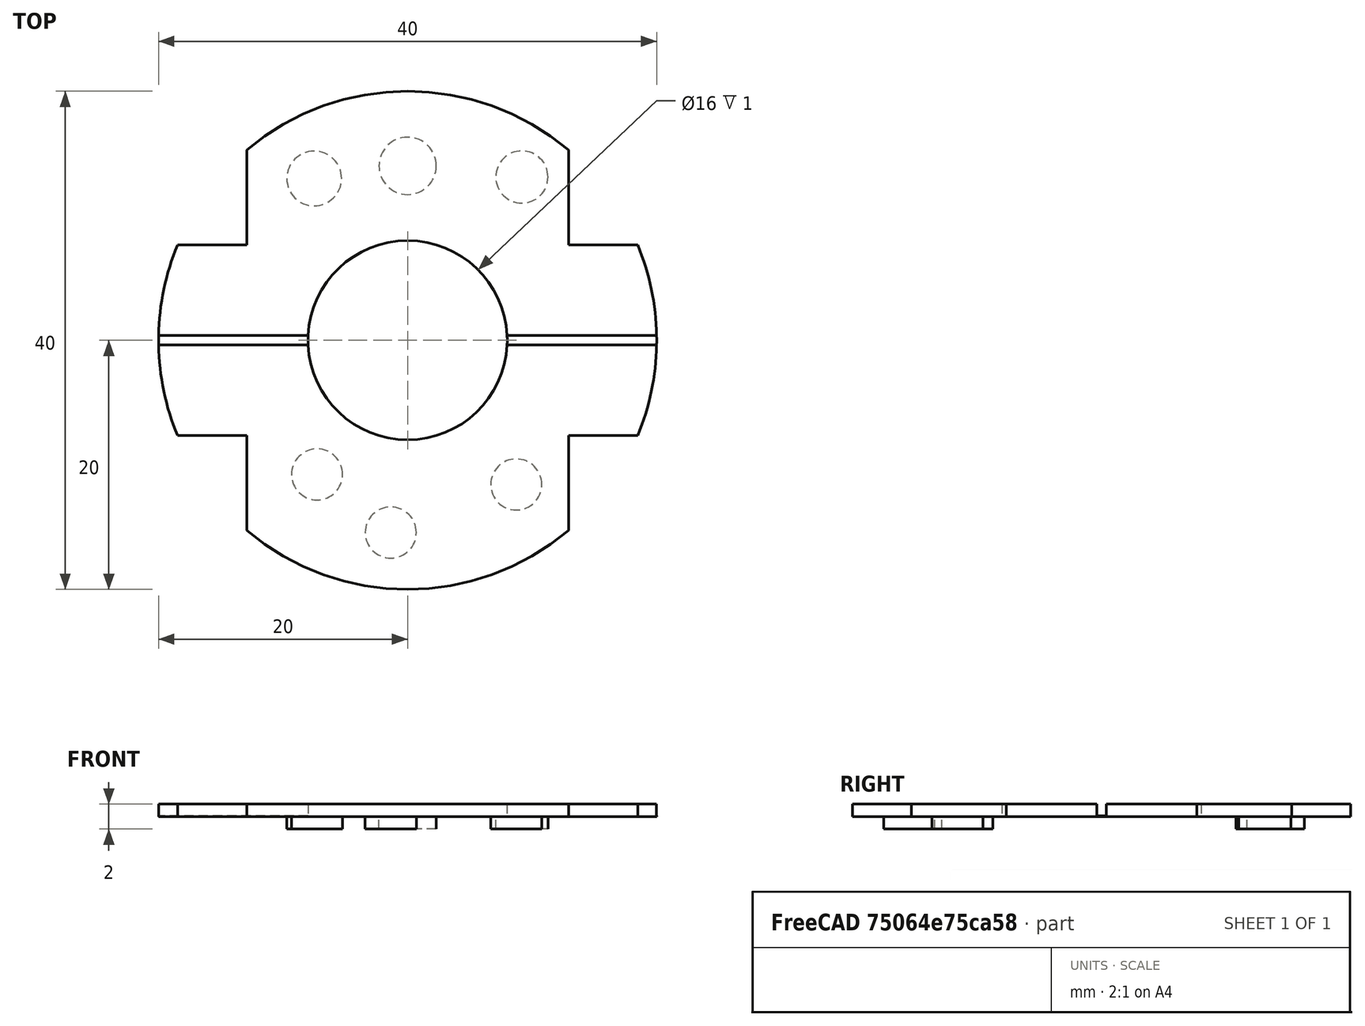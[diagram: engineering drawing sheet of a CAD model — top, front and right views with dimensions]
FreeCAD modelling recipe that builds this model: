
FCSTD DOCUMENT  (FreeCAD 0.19R)
Label: 3.9mmX16.GlueLID
License: All rights reserved
LicenseURL: http://en.wikipedia.org/wiki/All_rights_reserved
objects: Sketcher::SketchObject×4, PartDesign::Pad×2, PartDesign::Pocket×2, PartDesign::Body×1, Mesh::Feature×1
note: 13 computed .brp shape members not serialized (recipe doc carries the construction recipe); baked Part::Feature solids carry a one-line shape summary decoded from their .brp

FEATURE [Sketcher::SketchObject] Sketch
  FullyConstrained = true
  MapMode = 5
  sketch-geometry (2):
    g0: Circle CenterX=0 CenterY=0 CenterZ=0 NormalX=0 NormalY=0 NormalZ=1 AngleXU=0 Radius=20
    g1: Circle CenterX=0 CenterY=0 CenterZ=0 NormalX=0 NormalY=0 NormalZ=1 AngleXU=0 Radius=8
  constraints (4):
    c: Coincident(g0,g-1)
    c: Diameter(g0) = 40
    c: Diameter(g1) = 16
    c: Coincident(g1,g0)
FEATURE [PartDesign::Pad] Pad
  Direction = (1,1,1)
  Length = 1
  Length2 = 100
  Profile = -> Sketch
  Type = 0
FEATURE [Sketcher::SketchObject] Sketch001
  FullyConstrained = true
  MapMode = 5
  Placement = pos=(0,0,1) rot=(0,0,1;0rad)
  Support = -> [Pad]
  sketch-geometry (12):
    g0: Circle CenterX=0 CenterY=14 CenterZ=0 NormalX=0 NormalY=0 NormalZ=1 AngleXU=0 Radius=2.3
    g1: Circle CenterX=0 CenterY=14 CenterZ=0 NormalX=0 NormalY=0 NormalZ=1 AngleXU=0 Radius=1.95
    g2: LineSegment StartX=0 StartY=0 StartZ=0 EndX=14.609 EndY=20.8638 EndZ=0
    g3: LineSegment StartX=0 StartY=0 StartZ=0 EndX=-13.76 EndY=23.833 EndZ=0
    g4: Circle CenterX=-7.5 CenterY=12.9904 CenterZ=0 NormalX=0 NormalY=0 NormalZ=1 AngleXU=0 Radius=2.2
    g5: Circle CenterX=9.17722 CenterY=13.1064 CenterZ=0 NormalX=0 NormalY=0 NormalZ=1 AngleXU=0 Radius=2.1
    g6: LineSegment StartX=0 StartY=0 StartZ=0 EndX=-16.7758 EndY=-24.8711 EndZ=0
    g7: LineSegment StartX=0 StartY=0 StartZ=0 EndX=-1.92789 EndY=-22.0358 EndZ=0
    g8: LineSegment StartX=0 StartY=0 StartZ=0 EndX=15.1718 EndY=-20.1336 EndZ=0
    g9: Circle CenterX=8.72632 CenterY=-11.5802 CenterZ=0 NormalX=0 NormalY=0 NormalZ=1 AngleXU=0 Radius=2.05
    g10: Circle CenterX=-1.35091 CenterY=-15.441 CenterZ=0 NormalX=0 NormalY=0 NormalZ=1 AngleXU=0 Radius=2.05
    g11: Circle CenterX=-7.26951 CenterY=-10.7775 CenterZ=0 NormalX=0 NormalY=0 NormalZ=1 AngleXU=0 Radius=2.05
  constraints (35):
    c: PointOnObject(g0,g-2)
    c: DistanceY(g0) = 14
    c: Diameter(g0) = 4.6
    c: Diameter(g1) = 3.9
    c: Coincident(g1,g0)
    c: Coincident(g2,g-1)
    c: Coincident(g3,g2)
    c: PointOnObject(g5,g2)
    c: PointOnObject(g4,g3)
    c: Distance(g-1,g4) = 15
    c: Distance(g-1,g5) = 16
    c: Angle(g3) = 2.0944
    c: Angle(g2) = 0.959931
    c: Diameter(g4) = 4.4
    c: Diameter(g5) = 4.2
    c: Coincident(g6,g-1)
    c: Coincident(g7,g6)
    c: Coincident(g8,g6)
    c: PointOnObject(g11,g6)
    c: PointOnObject(g10,g7)
    c: PointOnObject(g9,g8)
    c: Distance(g-1,g9) = 14.5
    c: Distance(g-1,g10) = 15.5
    c: Distance(g-1,g11) = 13
    c: Diameter(g11) = 4.1
    c: Equal(g11,g10)
    c: Equal(g11,g9)
    c: Distance(g6) = 30
    c: Angle(g7) = -1.65806
    c: Angle(g6) = -2.16421
    c: Angle(g8) = -0.925025
    c: Distance(g8) = 25.21
    c: Distance(g2) = 25.47
    c: Distance(g3) = 27.52
    c: Distance(g7) = 22.12
FEATURE [PartDesign::Pad] Pad001
  BaseFeature = -> Pad
  Direction = (1,1,1)
  Length = 2
  Length2 = 100
  Profile = -> Sketch001
  Reversed = true
  Type = 0
FEATURE [Sketcher::SketchObject] Sketch004  label="slice"
  FullyConstrained = false
  MapMode = 5
  Placement = pos=(0,0,1) rot=(0,0,1;0rad)
  Support = -> [Pad001]
  sketch-geometry (4):
    g0: LineSegment StartX=-22.2478 StartY=0.375 StartZ=0 EndX=20.7748 EndY=0.375 EndZ=0
    g1: LineSegment StartX=20.7748 StartY=0.375 StartZ=0 EndX=20.7748 EndY=-0.375 EndZ=0
    g2: LineSegment StartX=20.7748 StartY=-0.375 StartZ=0 EndX=-22.2478 EndY=-0.375 EndZ=0
    g3: LineSegment StartX=-22.2478 StartY=-0.375 StartZ=0 EndX=-22.2478 EndY=0.375 EndZ=0
  constraints (9):
    c: Coincident(g0,g1)
    c: Coincident(g1,g2)
    c: Coincident(g2,g3)
    c: Coincident(g3,g0)
    c: Horizontal(g0)
    c: Horizontal(g2)
    c: Vertical(g3)
    c: Distance(g1) = 0.75
    c: Symmetric(g1,g0,g-1)
FEATURE [PartDesign::Pocket] Pocket
  BaseFeature = -> Pad001
  Length = 0.95
  Length2 = 100
  Profile = -> Sketch004
  Type = 0
FEATURE [Sketcher::SketchObject] Sketch007  label="notches"
  FullyConstrained = false
  MapMode = 5
  Placement = pos=(0,0,1) rot=(0,0,1;0rad)
  Support = -> [Pocket]
  sketch-geometry (16):
    g0: LineSegment StartX=-20.5587 StartY=-7.65293 StartZ=0 EndX=-12.9211 EndY=-7.65293 EndZ=0
    g1: LineSegment StartX=-12.9211 StartY=-7.65293 StartZ=0 EndX=-12.9211 EndY=-18.5136 EndZ=0
    g2: LineSegment StartX=-12.9211 StartY=-18.5136 StartZ=0 EndX=-20.5587 EndY=-18.5136 EndZ=0
    g3: LineSegment StartX=-20.5587 StartY=-18.5136 StartZ=0 EndX=-20.5587 EndY=-7.65293 EndZ=0
    g4: LineSegment StartX=-21.1657 StartY=19.7081 StartZ=0 EndX=-12.9211 EndY=19.7081 EndZ=0
    g5: LineSegment StartX=-12.9211 StartY=19.7081 StartZ=0 EndX=-12.9211 EndY=7.65293 EndZ=0
    g6: LineSegment StartX=-12.9211 StartY=7.65293 StartZ=0 EndX=-21.1657 EndY=7.65293 EndZ=0
    g7: LineSegment StartX=-21.1657 StartY=7.65293 StartZ=0 EndX=-21.1657 EndY=19.7081 EndZ=0
    g8: LineSegment StartX=12.9211 StartY=18.5942 StartZ=0 EndX=21.451 EndY=18.5942 EndZ=0
    g9: LineSegment StartX=21.451 StartY=18.5942 StartZ=0 EndX=21.451 EndY=7.65293 EndZ=0
    g10: LineSegment StartX=21.451 StartY=7.65293 StartZ=0 EndX=12.9211 EndY=7.65293 EndZ=0
    g11: LineSegment StartX=12.9211 StartY=7.65293 StartZ=0 EndX=12.9211 EndY=18.5942 EndZ=0
    g12: LineSegment StartX=12.9211 StartY=-7.65293 StartZ=0 EndX=24.754 EndY=-7.65293 EndZ=0
    g13: LineSegment StartX=24.754 StartY=-7.65293 StartZ=0 EndX=24.754 EndY=-18.3213 EndZ=0
    g14: LineSegment StartX=24.754 StartY=-18.3213 StartZ=0 EndX=12.9211 EndY=-18.3213 EndZ=0
    g15: LineSegment StartX=12.9211 StartY=-18.3213 StartZ=0 EndX=12.9211 EndY=-7.65293 EndZ=0
  constraints (35):
    c: Coincident(g0,g1)
    c: Coincident(g1,g2)
    c: Coincident(g2,g3)
    c: Coincident(g3,g0)
    c: Horizontal(g0)
    c: Horizontal(g2)
    c: Vertical(g1)
    c: Vertical(g3)
    c: Coincident(g4,g5)
    c: Coincident(g5,g6)
    c: Coincident(g6,g7)
    c: Coincident(g7,g4)
    c: Horizontal(g4)
    c: Horizontal(g6)
    c: Vertical(g5)
    c: Vertical(g7)
    c: Coincident(g8,g9)
    c: Coincident(g9,g10)
    c: Coincident(g10,g11)
    c: Coincident(g11,g8)
    c: Horizontal(g8)
    c: Horizontal(g10)
    c: Vertical(g9)
    c: Vertical(g11)
    c: Coincident(g12,g13)
    c: Coincident(g13,g14)
    c: Coincident(g14,g15)
    c: Coincident(g15,g12)
    c: Horizontal(g12)
    c: Horizontal(g14)
    c: Vertical(g13)
    c: Vertical(g15)
    c: Symmetric(g12,g0,g-2)
    c: Symmetric(g10,g0,g-1)
    c: Symmetric(g5,g12,g-1)
FEATURE [PartDesign::Pocket] Pocket001
  BaseFeature = -> Pocket
  Length = 5
  Length2 = 100
  Profile = -> Sketch007
  Type = 0
FEATURE [PartDesign::Body] Body
  Group = -> [Sketch,Sketch001,Sketch004,Sketch007,Pad,Pad001,Pocket,Pocket001]
  Origin = -> Origin
  Tip = -> Pocket001
FEATURE [Mesh::Feature] Mesh  label="Pocket001 (Meshed)"
